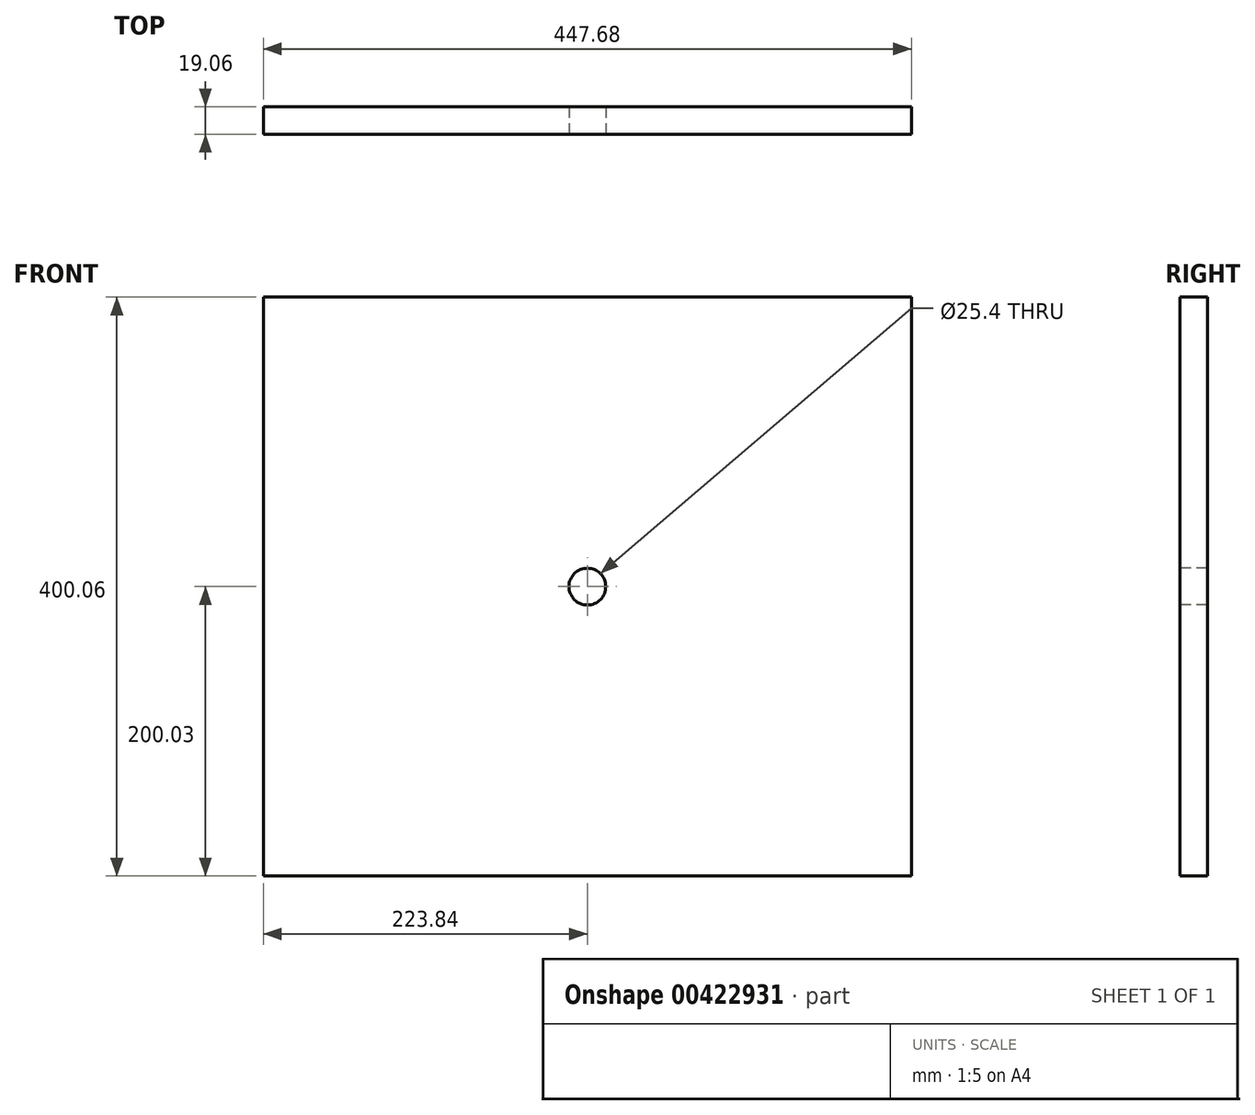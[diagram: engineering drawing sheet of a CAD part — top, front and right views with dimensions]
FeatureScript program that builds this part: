
annotation { "Feature Type Name" : "Feature", "Feature Type Description" : "" }
export const myFeature = defineFeature(function(context is Context, id is Id, definition is map)
    precondition{}
    {
        {
            var Q0;
            Q0=qCreatedBy(makeId("Front.planeOp"),FACE);
            var sketch = newSketch(context, id + "F0", { "sketchPlane" : qUnion([Q0])});
            skLineSegment(sketch, "E0.bottom", {"start": v(223.84, 200.03) * mm, "end": v(-223.84, 200.03) * mm});
            skLineSegment(sketch, "E0.top", {"start": v(223.84, -200.03) * mm, "end": v(-223.84, -200.03) * mm});
            skLineSegment(sketch, "E0.left", {"start": v(223.84, 200.03) * mm, "end": v(223.84, -200.03) * mm});
            skLineSegment(sketch, "E0.right", {"start": v(-223.84, 200.03) * mm, "end": v(-223.84, -200.03) * mm});
            skPoint(sketch, "E0.middle", {"position": v(0, 0) * mm});
            skSolve(sketch);
        }
        {
            var Q0;
            Q0=makeQuery(id+"F0.imprint","IMPRINT",FACE,{"disambiguationData":[TD([[makeQuery(id+"F0.imprint","IMPRINT",EDGE,{"derivedFrom":sQuery(id+"F0.wireOp",EDGE,"E0.bottom")}),1.0]])]});
            extrude(context, id + "F1", {"entities" : qUnion([Q0]), "endBound" : BoundingType.SYMMETRIC, "depth" : 19.05 * mm});
        }
        {
            var Q0;
            Q0=makeQuery(id+"F1.opExtrude","CAP_FACE",FACE,{"disambiguationData":[OSD([sQuery(id+"F0.wireOp",EDGE,"E0.bottom"),sQuery(id+"F0.wireOp",EDGE,"E0.top"),sQuery(id+"F0.wireOp",EDGE,"E0.left"),sQuery(id+"F0.wireOp",EDGE,"E0.right")])],"isStart":false});
            var sketch = newSketch(context, id + "F2", { "sketchPlane" : qUnion([Q0])});
            skCircle(sketch, "E1", {"center": v(0, 0) * mm, "radius": 12.7 * mm});
            skSolve(sketch);
        }
        {
            var Q0;
            Q0 = qSketchRegion(id + "F2", true);
            extrude(context, id + "F3", {"entities" : qUnion([Q0]), "operationType" : NewBodyOperationType.REMOVE, "oppositeDirection" : true, "depth" : 25.4 * mm});
        }
    });
